# Revit family: Gohome_UtilityChair_R21
name_source: partatom
category: Furniture
units: mm (PartAtom-declared; Revit-internal decimal feet)

## family parameters
Always vertical = Yes
Cut with Voids When Loaded = No
OmniClass Number = 23.40.20.00
OmniClass Title = General Furniture and Specialties
Room Calculation Point = No
Shared = No
Work Plane-Based = No

## types (2) — shared parameters
Backrest Material = <By Category>
Depth = 540 mm  [stored 1.77165 ft]
Frame Material = <By Category>
Height = 760 mm
Manufacturer = gohome
Model = Utility Chair
Seat Height = 450 mm  [stored 1.47638 ft]
Seat Material = <By Category>
URL = www.gohome.com.au
Upholstered Backrest Material = <By Category>
Width = 462 mm  [stored 1.51575 ft]
zero-valued in all types: Default Elevation

## per-type parameters (varying)
| type | Upholstered Backrest |
| With Upholstered Backrest | Yes |
| Plywood Backrest | No |

note: [stored X ft] marks values corroborated as IEEE doubles in the binary element streams (Revit-internal decimal feet)

## geometry (parser evidence)
native form markers: Sweep x2
no freeform markers — native parametric forms only
